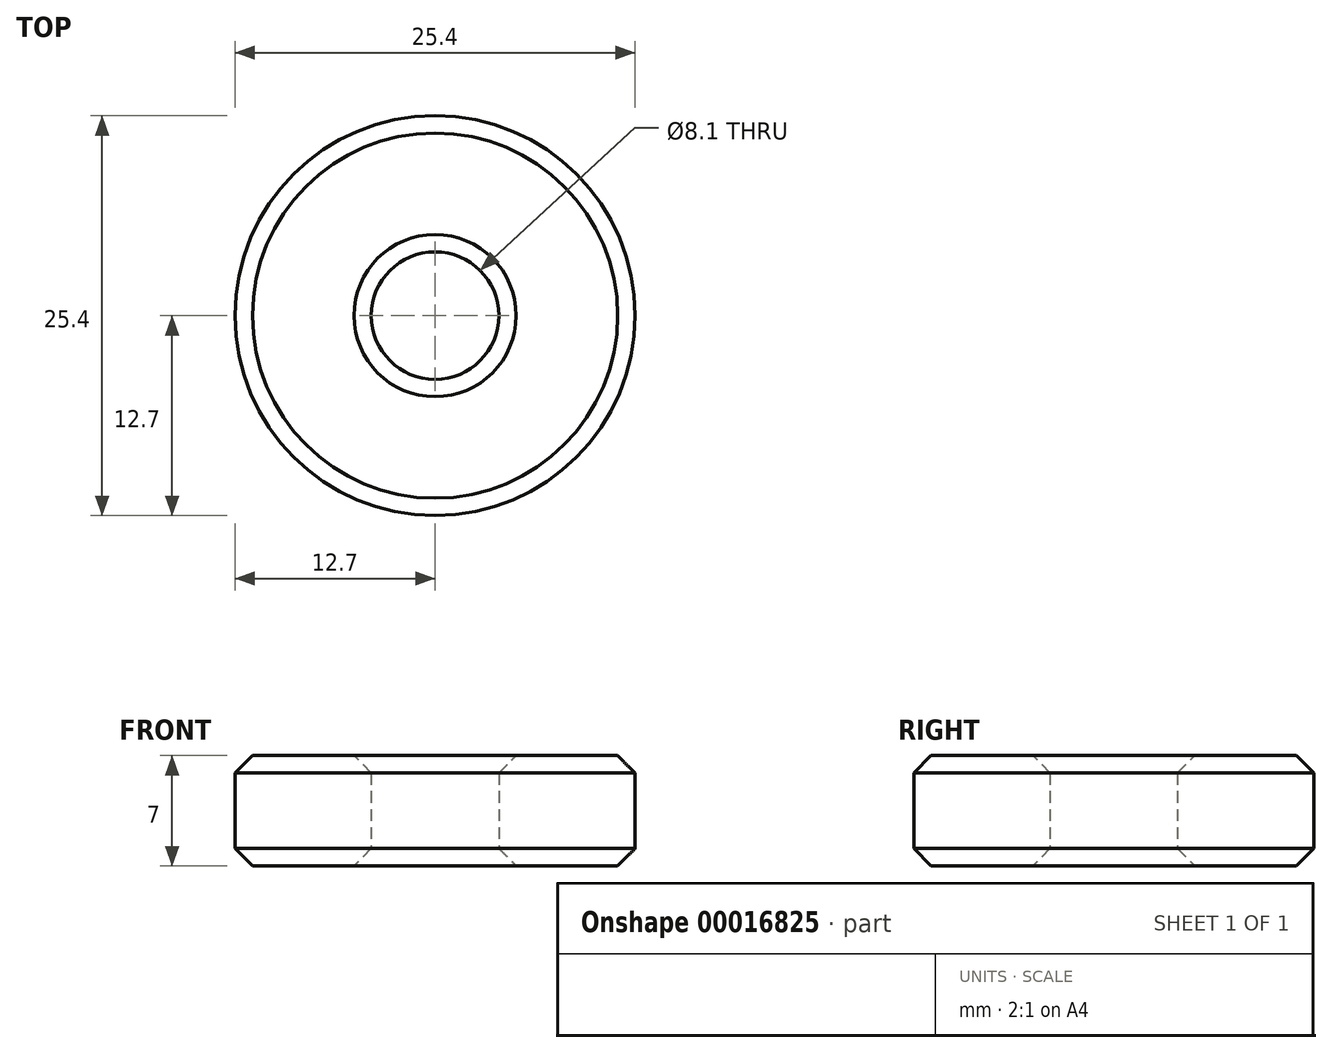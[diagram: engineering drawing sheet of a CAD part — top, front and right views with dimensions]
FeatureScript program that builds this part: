
annotation { "Feature Type Name" : "Feature", "Feature Type Description" : "" }
export const myFeature = defineFeature(function(context is Context, id is Id, definition is map)
    precondition{}
    {
        {
            var Q0;
            Q0=qCreatedBy(makeId("Top.planeOp"),FACE);
            var sketch = newSketch(context, id + "F0", { "sketchPlane" : qUnion([Q0])});
            skCircle(sketch, "E0", {"center": v(0, 0) * mm, "radius": 12.7 * mm});
            skCircle(sketch, "E1", {"center": v(0, 0) * mm, "radius": 4.05 * mm});
            skSolve(sketch);
        }
        {
            var Q0;
            Q0 = qSketchRegion(id + "F0", true);
            extrude(context, id + "F1", {"entities" : qUnion([Q0]), "depth" : 7 * mm});
        }
        {
            var Q0;
            Q0=makeQuery(id+"F1.opExtrude","CAP_FACE",FACE,{"disambiguationData":[OSD([sQuery(id+"F0.wireOp",EDGE,"E0"),sQuery(id+"F0.wireOp",EDGE,"E1")])],"isStart":false});
            var Q1;
            Q1=makeQuery(id+"F1.opExtrude","CAP_FACE",FACE,{"disambiguationData":[OSD([sQuery(id+"F0.wireOp",EDGE,"E0"),sQuery(id+"F0.wireOp",EDGE,"E1")])],"isStart":true});
            chamfer(context, id + "F2", {"entities" : qUnion([Q0, Q1]), "width" : 1.1 * mm, "tangentPropagation" : true});
        }
    });
